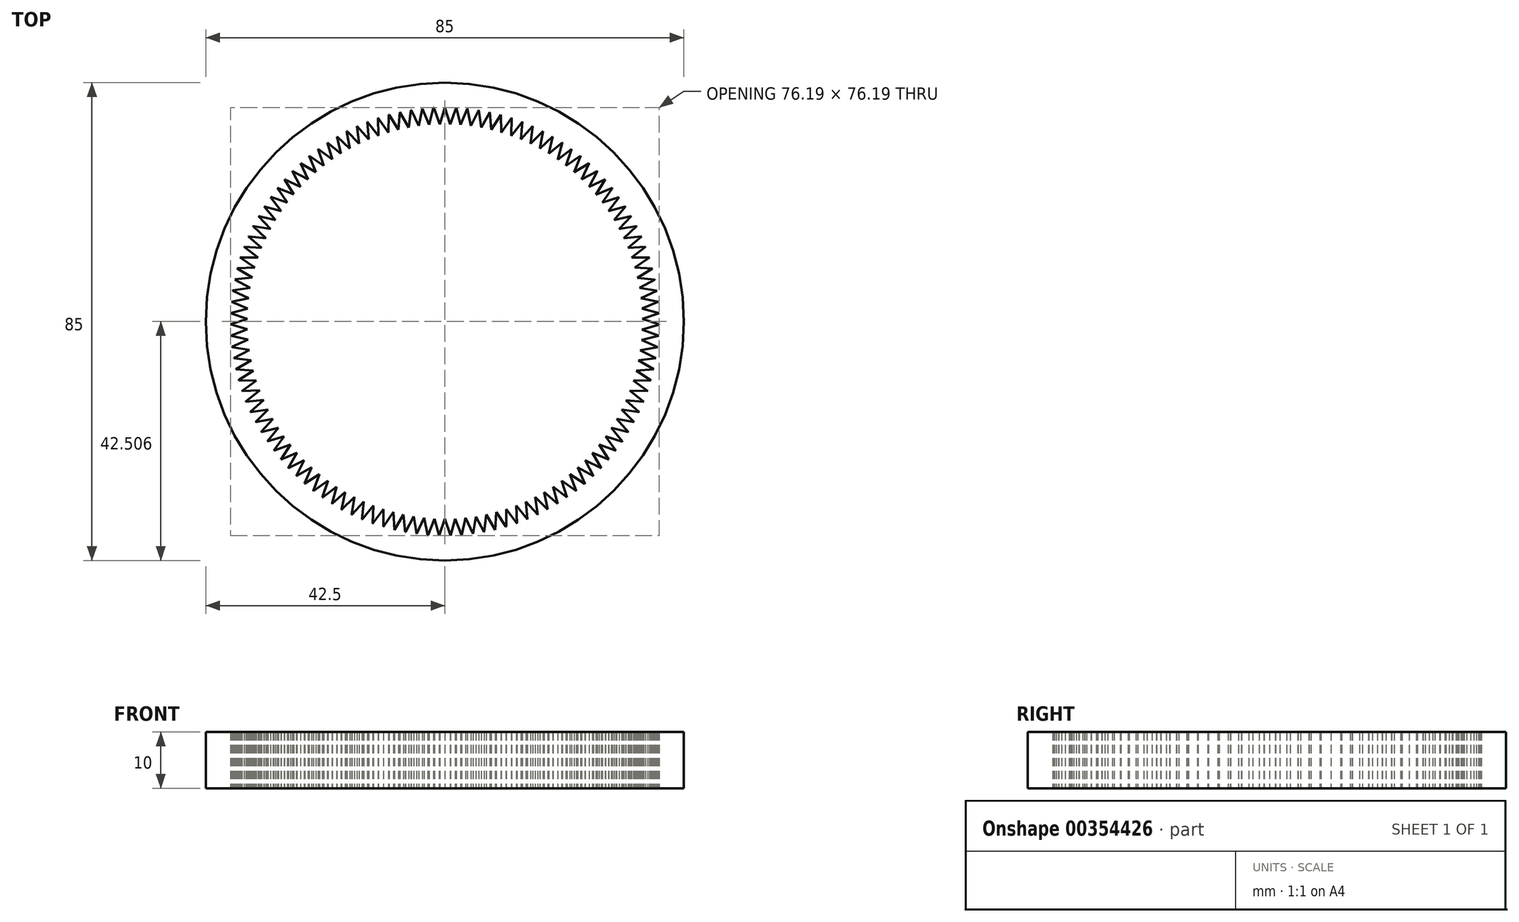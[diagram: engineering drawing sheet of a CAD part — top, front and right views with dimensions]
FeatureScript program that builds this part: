
annotation { "Feature Type Name" : "Feature", "Feature Type Description" : "" }
export const myFeature = defineFeature(function(context is Context, id is Id, definition is map)
    precondition{}
    {
        {
            var Q0;
            Q0=qCreatedBy(makeId("Top.planeOp"),FACE);
            var sketch = newSketch(context, id + "F0", { "sketchPlane" : qUnion([Q0])});
            skCircle(sketch, "E0", {"center": v(0, 0) * mm, "radius": 38.1 * mm});
            skCircle(sketch, "E1", {"center": v(0, 0) * mm, "radius": 42.5 * mm});
            skLineSegment(sketch, "E2", {"start": v(0, 0) * mm, "end": v(0, 59.15) * mm, "construction": true});
            skLineSegment(sketch, "E3", {"start": v(0, 0) * mm, "end": v(-3.13, 59.79) * mm, "construction": true});
            skLineSegment(sketch, "E4", {"start": v(0, 38.1) * mm, "end": v(0, 35.1) * mm});
            skLineSegment(sketch, "E5", {"start": v(0, 35.1) * mm, "end": v(-1.84, 35.1) * mm, "construction": true});
            skLineSegment(sketch, "E6", {"start": v(-1.84, 35.1) * mm, "end": v(-2, 38.05) * mm});
            skLineSegment(sketch, "E7", {"start": v(-2, 38.05) * mm, "end": v(-0.92, 35.1) * mm});
            skLineSegment(sketch, "E8", {"start": v(-0.92, 35.1) * mm, "end": v(0, 38.1) * mm});
            skSolve(sketch);
        }
        {
            var Q0;
            Q0=makeQuery(id+"F0.imprint","IMPRINT",FACE,{"disambiguationData":[TD([[makeQuery(id+"F0.imprint","IMPRINT",EDGE,{"derivedFrom":sQuery(id+"F0.wireOp",EDGE,"E1")}),1.0]])]});
            var Q1;
            {var subQ2=sQuery(id+"F0.wireOp",EDGE,"E7");Q1=makeQuery(id+"F0.imprint","IMPRINT",FACE,{"disambiguationData":[TD([[makeQuery(id+"F0.imprint","IMPRINT",EDGE,{"derivedFrom":subQ2}),1.0]])]});}
            extrude(context, id + "F1", {"entities" : qUnion([Q0, Q1]), "depth" : 10 * mm});
        }
        {
            var Q0;
            Q0=makeQuery(id+"F1.opExtrude","SWEPT_FACE",FACE,{"disambiguationData":[OSD([sQuery(id+"F0.wireOp",EDGE,"E7")])]});
            var Q1;
            Q1=makeQuery(id+"F1.opExtrude","SWEPT_FACE",FACE,{"disambiguationData":[OSD([sQuery(id+"F0.wireOp",EDGE,"E8")])]});
            var Q2;
            Q2=makeQuery(id+"F1.opExtrude","SWEPT_FACE",FACE,{"disambiguationData":[OSD([sQuery(id+"F0.wireOp",EDGE,"E0")])]});
            circularPattern(context, id + "F2", {"patternType" : PatternType.FACE, "faces" : qUnion([Q0, Q1]), "axis" : qUnion([Q2]), "angle" : 360 * degree, "instanceCount" : 119, "equalSpace" : true});
        }
    });
